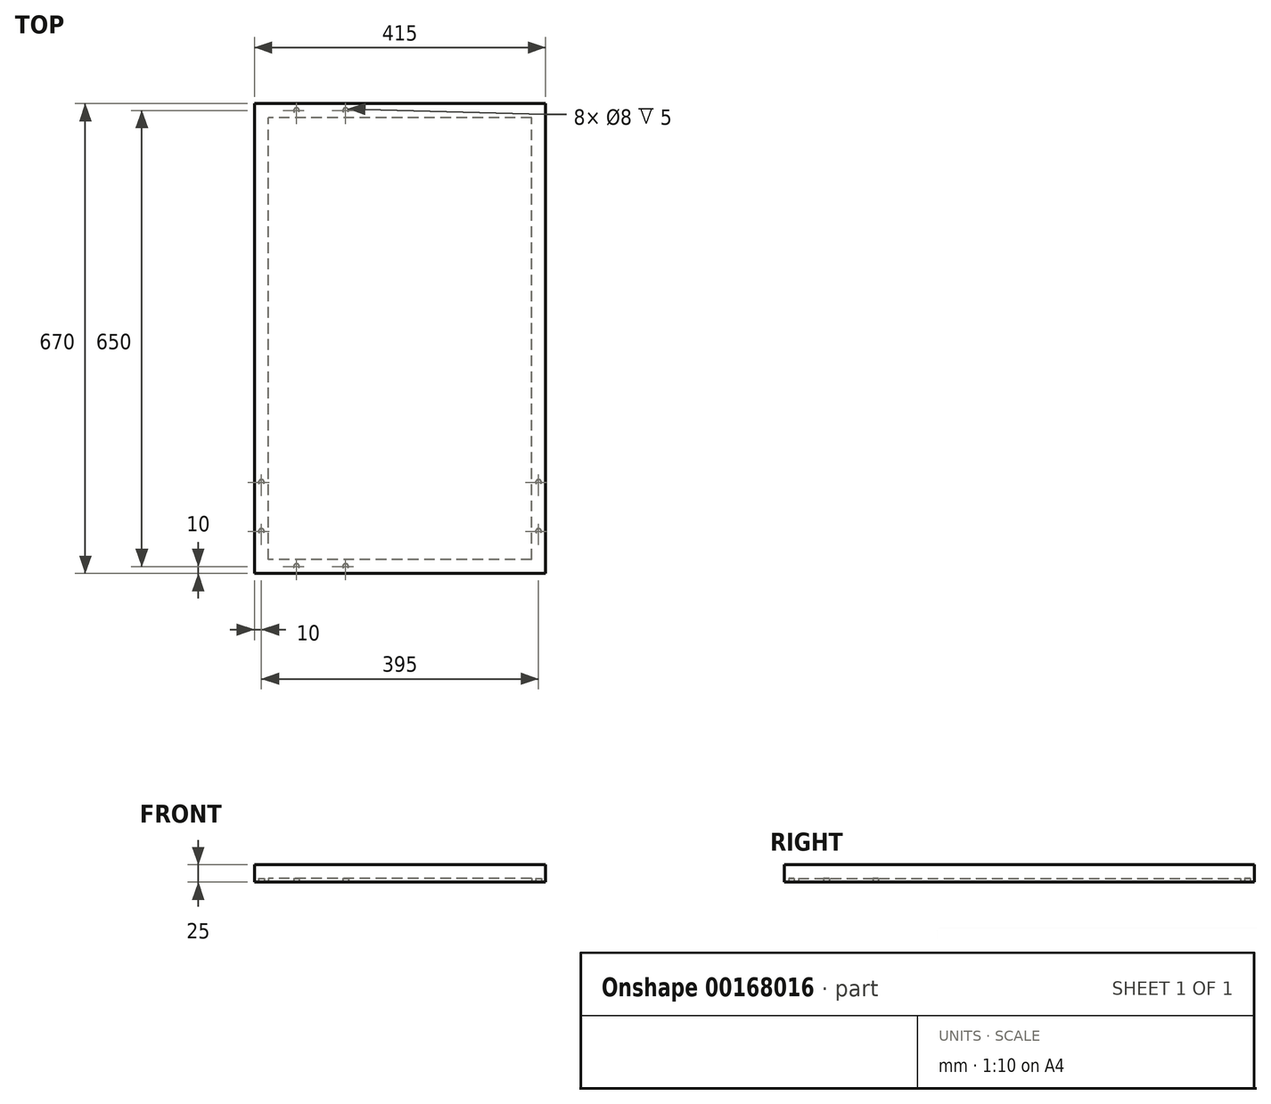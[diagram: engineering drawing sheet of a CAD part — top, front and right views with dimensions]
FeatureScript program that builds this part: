
annotation { "Feature Type Name" : "Feature", "Feature Type Description" : "" }
export const myFeature = defineFeature(function(context is Context, id is Id, definition is map)
    precondition{}
    {
        {
            var Q0;
            Q0=qCreatedBy(makeId("Top.planeOp"),FACE);
            var sketch = newSketch(context, id + "F0", { "sketchPlane" : qUnion([Q0])});
            skLineSegment(sketch, "E0.bottom", {"start": v(207.5, -335) * mm, "end": v(-207.5, -335) * mm});
            skLineSegment(sketch, "E0.top", {"start": v(207.5, 335) * mm, "end": v(-207.5, 335) * mm});
            skLineSegment(sketch, "E0.left", {"start": v(207.5, -335) * mm, "end": v(207.5, 335) * mm});
            skLineSegment(sketch, "E0.right", {"start": v(-207.5, -335) * mm, "end": v(-207.5, 335) * mm});
            skPoint(sketch, "E0.middle", {"position": v(0, 0) * mm});
            skSolve(sketch);
        }
        {
            var Q0;
            Q0=qSketchRegion(id+"F0",true);
            extrude(context, id + "F1", {"entities" : qUnion([Q0]), "depth" : 25 * mm});
        }
        {
            var Q0;
            Q0=makeQuery(id+"F1.opExtrude","CAP_FACE",FACE,{"disambiguationData":[OSD([sQuery(id+"F0.wireOp",EDGE,"E0.bottom"),sQuery(id+"F0.wireOp",EDGE,"E0.top"),sQuery(id+"F0.wireOp",EDGE,"E0.left"),sQuery(id+"F0.wireOp",EDGE,"E0.right")])],"isStart":true});
            shell(context, id + "F2", {"entities" : qUnion([Q0]), "thickness" : 20 * mm});
        }
        {
            var Q0;
            Q0=makeQuery(id+"F1.opExtrude","CAP_FACE",FACE,{"disambiguationData":[OSD([sQuery(id+"F0.wireOp",EDGE,"E0.bottom"),sQuery(id+"F0.wireOp",EDGE,"E0.top"),sQuery(id+"F0.wireOp",EDGE,"E0.left"),sQuery(id+"F0.wireOp",EDGE,"E0.right")])],"isStart":true});
            var sketch = newSketch(context, id + "F3", { "sketchPlane" : qUnion([Q0])});
            skCircle(sketch, "E1", {"center": v(-197.5, 275) * mm, "radius": 4 * mm});
            skCircle(sketch, "E2", {"center": v(-197.5, 205) * mm, "radius": 4 * mm});
            skCircle(sketch, "E3.MirrorC", {"center": v(197.5, 275) * mm, "radius": 4 * mm});
            skCircle(sketch, "E4.MirrorC", {"center": v(197.5, 205) * mm, "radius": 4 * mm});
            skCircle(sketch, "E5", {"center": v(-147.5, 325) * mm, "radius": 4 * mm});
            skCircle(sketch, "E6", {"center": v(-77.5, 325) * mm, "radius": 4 * mm});
            skCircle(sketch, "E7.MirrorC", {"center": v(-77.5, -325) * mm, "radius": 4 * mm});
            skCircle(sketch, "E8.MirrorC", {"center": v(-147.5, -325) * mm, "radius": 4 * mm});
            skSolve(sketch);
        }
        {
            var Q0;
            Q0=qSketchRegion(id+"F3",true);
            extrude(context, id + "F4", {"entities" : qUnion([Q0]), "operationType" : NewBodyOperationType.REMOVE, "oppositeDirection" : true, "depth" : 5 * mm});
        }
    });
